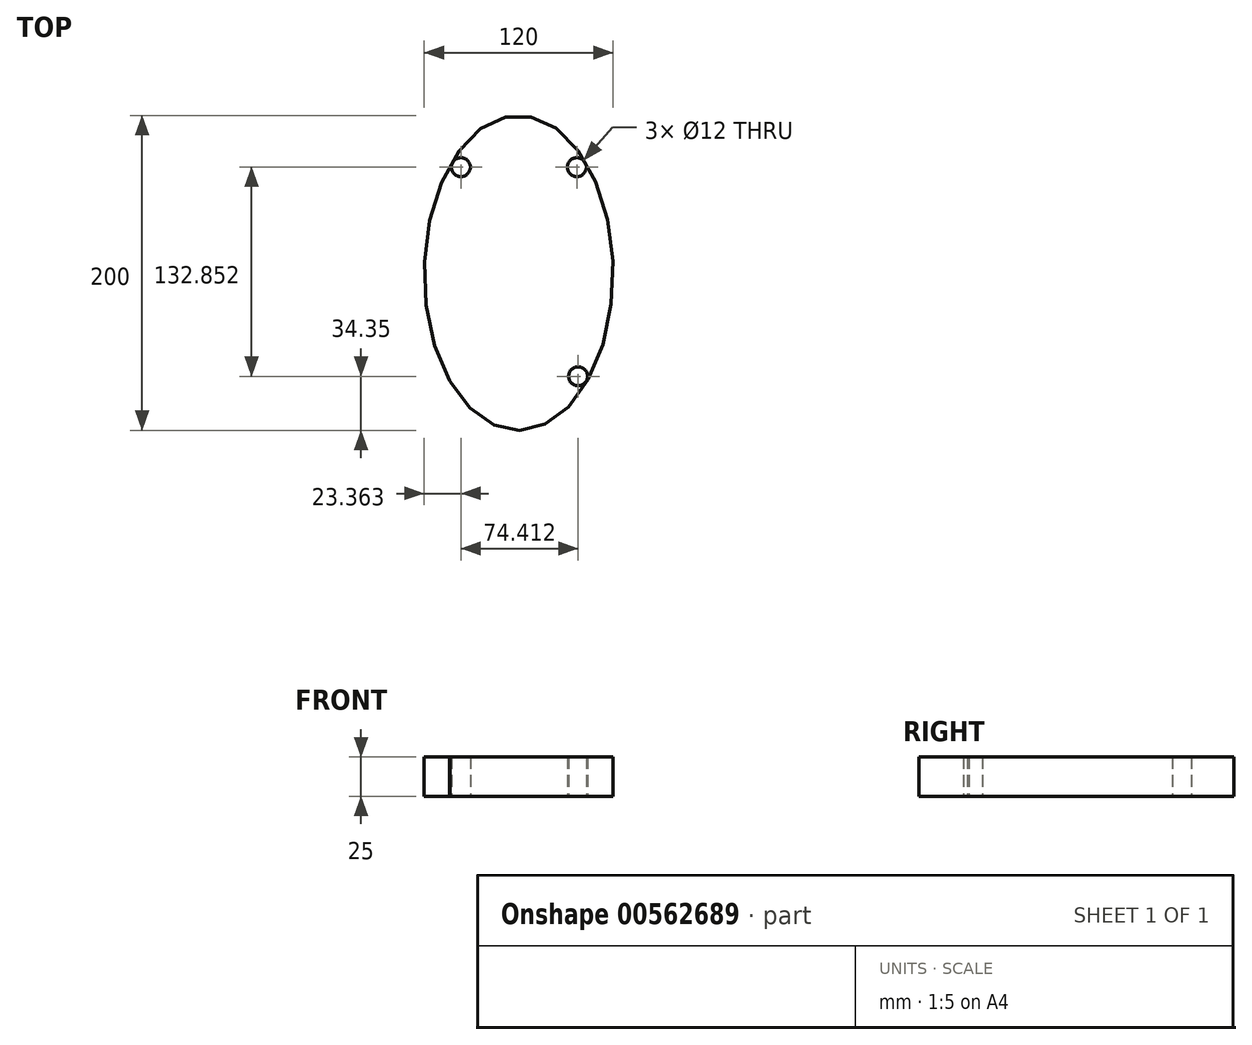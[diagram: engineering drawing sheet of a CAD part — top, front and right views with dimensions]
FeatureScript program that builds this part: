
annotation { "Feature Type Name" : "Feature", "Feature Type Description" : "" }
export const myFeature = defineFeature(function(context is Context, id is Id, definition is map)
    precondition{}
    {
        {
            var Q0;
            Q0=qCreatedBy(makeId("Top.planeOp"),FACE);
            var sketch = newSketch(context, id + "F0", { "sketchPlane" : qUnion([Q0])});
            skEllipse(sketch, "E0", {"center": v(0, 0) * mm, "majorRadius": 100 * mm, "minorRadius": 60 * mm, "majorAxis": v(0, 1)});
            skCircle(sketch, "E1", {"center": v(37.05, 67.2) * mm, "radius": 6 * mm});
            skCircle(sketch, "E2", {"center": v(-36.64, 67.2) * mm, "radius": 6 * mm});
            skCircle(sketch, "E3", {"center": v(-38.45, -65.65) * mm, "radius": 6 * mm});
            skCircle(sketch, "E4", {"center": v(37.78, -65.65) * mm, "radius": 6 * mm});
            skSolve(sketch);
        }
        {
            var Q0;
            Q0 = qSketchRegion(id + "F0", true);
            extrude(context, id + "F1", {"entities" : qUnion([Q0]), "depth" : 25 * mm, "offsetDistance" : 25 * mm});
        }
    });
